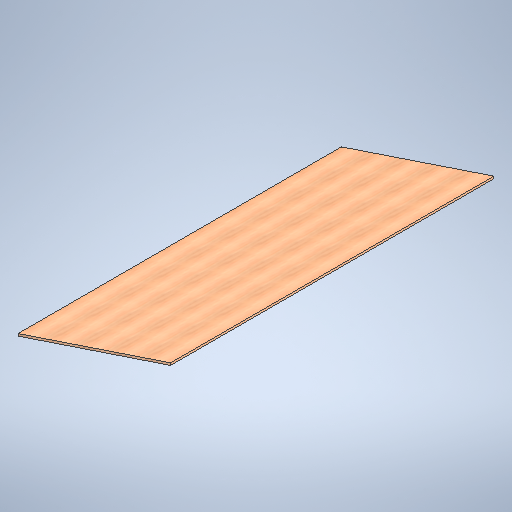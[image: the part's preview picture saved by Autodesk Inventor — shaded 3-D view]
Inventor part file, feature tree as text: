
AUTODESK INVENTOR PART (.ipt)
format: ipt  version: 2025 (Build 290162010, 162A)  size: 312,832 bytes
history: native  units: in
note: dims shown in document units (in); Inventor stores cm internally (conversion verified against a paired STEP export)
features: extrude x1, plane x1, sketch x1
ambient origin geometry x8: Origin, YZ Plane, XZ Plane, XY Plane, X Axis, Y Axis, Z Axis, Center Point
bodies: Body1 (feature_tree)
feature tree (3):
  extrude  "Extrusion2"  Depth=0.625in
  plane  "Work Plane2"
  sketch  "Sketch1"  dims[d5=5.5in d17=3.5in d19=132.0in d23=2.2565in d28=1.8188in d33=42.875in d36=0.625in d37=48.0in d38=96.0in d39=0.0in d40=90.0deg d41=0.625in d42=47.725in]
